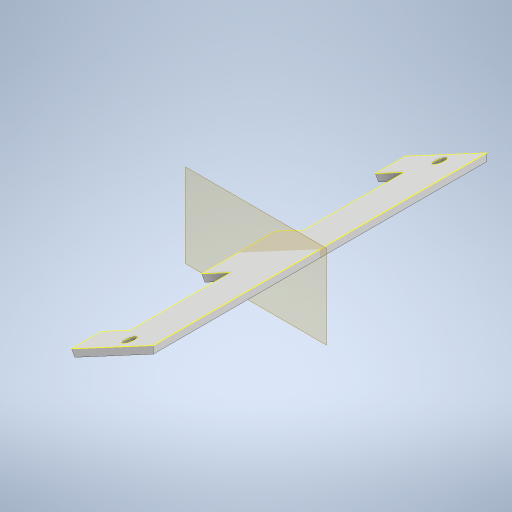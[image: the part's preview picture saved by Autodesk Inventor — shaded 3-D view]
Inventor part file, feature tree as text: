
AUTODESK INVENTOR PART (.ipt)
format: ipt  version: 2023 (Build 270158000, 158)  size: 305,664 bytes
history: native  units: in
note: dims shown in document units (in); Inventor stores cm internally (conversion verified against a paired STEP export)
features: other x9, reference x8, sketch x5, extrude x4, projected_geometry x2, mirror x1
ambient origin geometry x8: Origin, YZ Plane, XZ Plane, XY Plane, X Axis, Y Axis, Z Axis, Center Point
bodies: Body1 (feature_tree)
feature tree (29):
  other  "Bryła1"
  extrude  "Wyciągnięcie proste1"  Depth=3.937in
  extrude  "Wyciągnięcie proste4"  Depth=3.937in TaperAngle=0.0deg
  other  "Płaszczyzna konstrukcyjna1"
  mirror  "Odbij1"
  extrude  "Wyciągnięcie proste5"  Depth=0.0197in
  extrude  "Wyciągnięcie proste6"  Depth=0.0197in
  sketch  "Szkic8"
  sketch  "Szkic1"
  reference  "Odniesienie1"
  reference  "Odniesienie2"
  reference  "Odniesienie3"
  reference  "Odniesienie4"
  sketch  "Szkic5"
  reference  "Odniesienie15"
  reference  "Odniesienie16"
  reference  "Odniesienie17"
  sketch  "Szkic6"
  reference  "Odniesienie18"
  sketch  "Szkic7"
  projected_geometry  "Pętla rzutowana3"
  projected_geometry  "Pętla rzutowana4"
  other  "<userpath>\Desktop\MojeRoboty\Stefan\mechanics 2\STEFAN.iam"
  other  "STEFAN.iam"
  other  "podstawa:1"
  other  "koło_minisumo:2"
  other  "plug_nowy:1"
  other  "mocowanie sharpow:1"
  other  "plug_kopia:1"
